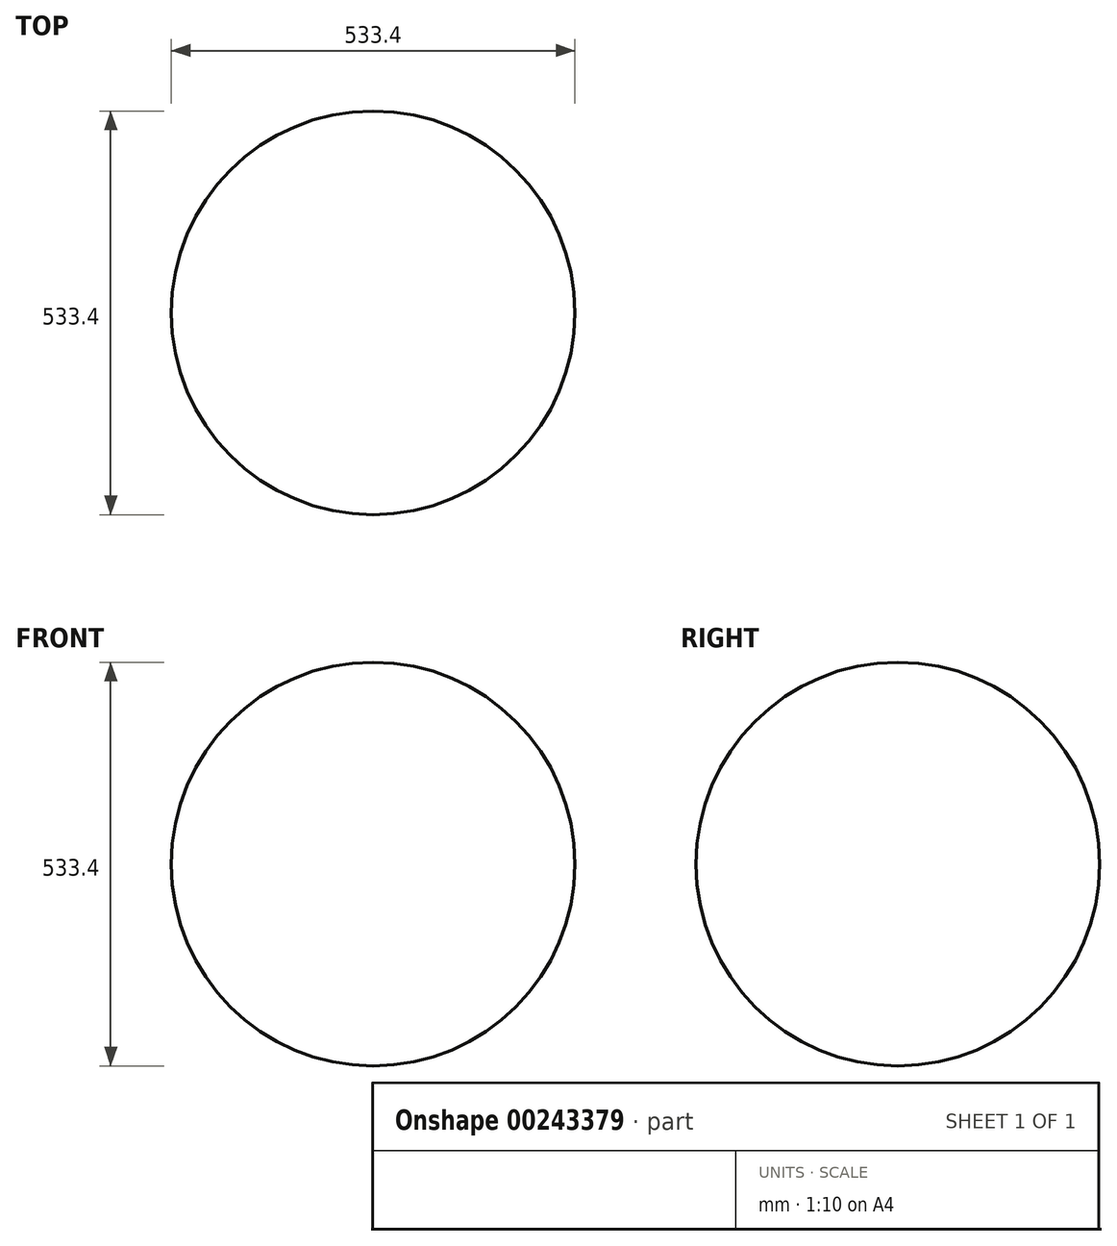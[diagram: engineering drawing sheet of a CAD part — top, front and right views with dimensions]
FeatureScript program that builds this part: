
annotation { "Feature Type Name" : "Feature", "Feature Type Description" : "" }
export const myFeature = defineFeature(function(context is Context, id is Id, definition is map)
    precondition{}
    {
        {
            var Q0;
            Q0=qCreatedBy(makeId("Front.planeOp"),FACE);
            var sketch = newSketch(context, id + "F0", { "sketchPlane" : qUnion([Q0])});
            skArc(sketch, "E0", {"start": v(0, -266.7) * mm, "mid": v(266.7, 0) * mm, "end": v(0, 266.7) * mm});
            skLineSegment(sketch, "E1", {"start": v(0, 266.7) * mm, "end": v(0, -266.7) * mm});
            skSolve(sketch);
        }
        {
            var Q0;
            Q0 = qSketchRegion(id + "F0", true);
            var Q1;
            Q1=sQuery(id+"F0.wireOp",EDGE,"E1");
            revolve(context, id + "F1", {"entities" : qUnion([Q0]), "axis" : qUnion([Q1]), "revolveType" : RevolveType.FULL});
        }
    });
